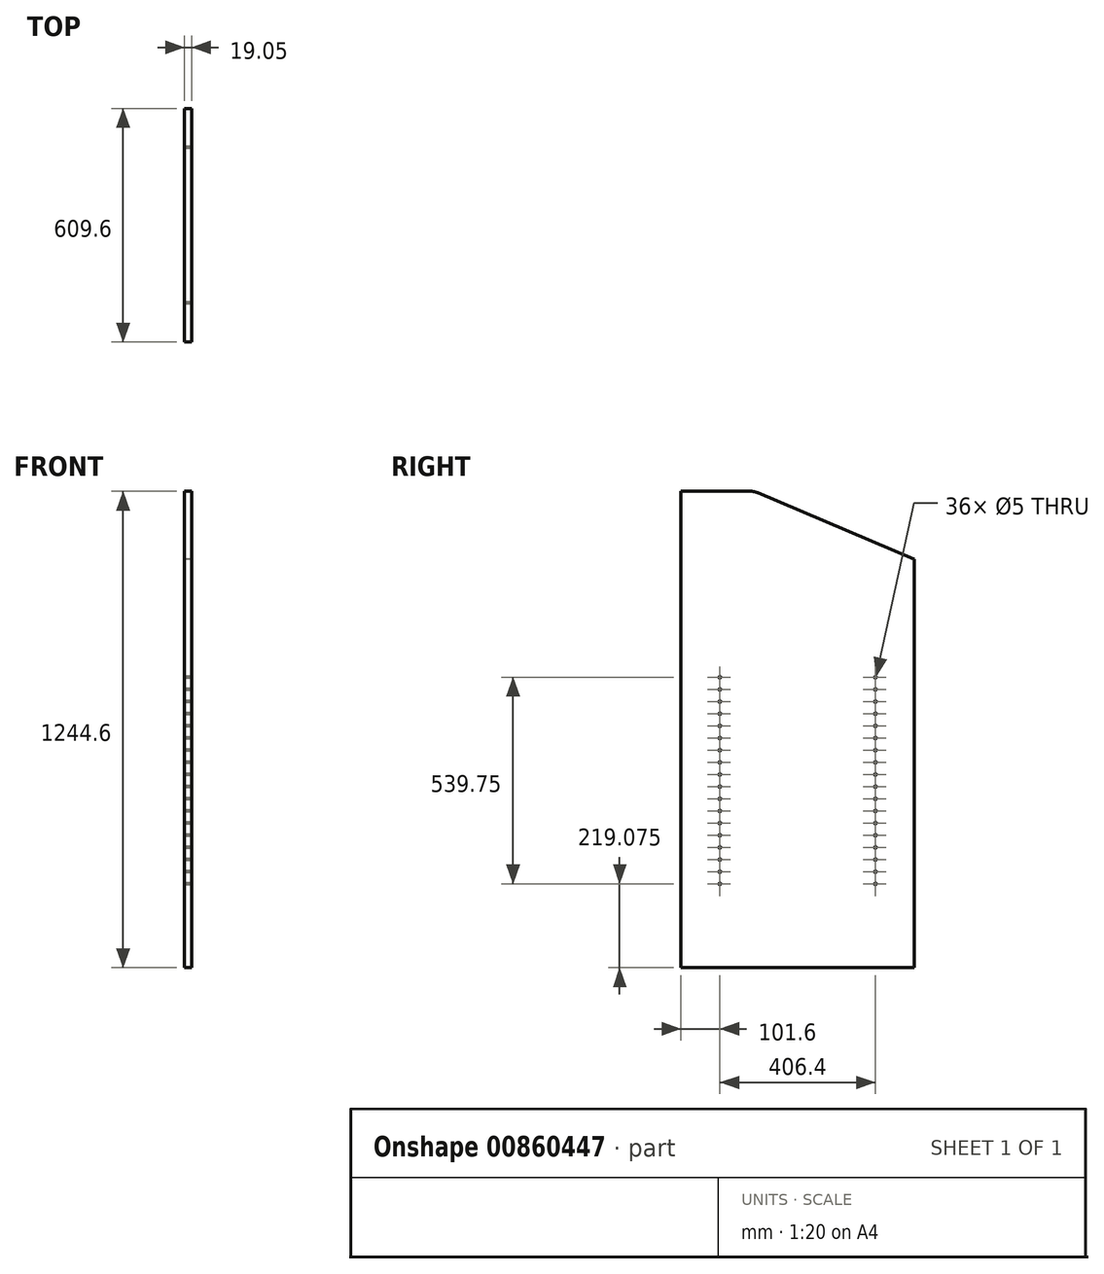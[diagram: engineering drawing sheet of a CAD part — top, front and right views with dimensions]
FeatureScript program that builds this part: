
annotation { "Feature Type Name" : "Feature", "Feature Type Description" : "" }
export const myFeature = defineFeature(function(context is Context, id is Id, definition is map)
    precondition{}
    {
        {
            var Q0;
            Q0=qCreatedBy(makeId("Right.planeOp"),FACE);
            var sketch = newSketch(context, id + "F0", { "sketchPlane" : qUnion([Q0])});
            skLineSegment(sketch, "E0.bottom", {"start": v(304.8, 622.3) * mm, "end": v(-304.8, 622.3) * mm});
            skLineSegment(sketch, "E0.top", {"start": v(304.8, -622.3) * mm, "end": v(-304.8, -622.3) * mm});
            skLineSegment(sketch, "E0.left", {"start": v(304.8, 622.3) * mm, "end": v(304.8, -622.3) * mm});
            skLineSegment(sketch, "E0.right", {"start": v(-304.8, 622.3) * mm, "end": v(-304.8, -622.3) * mm});
            skPoint(sketch, "E0.middle", {"position": v(0, 0) * mm});
            skLineSegment(sketch, "E1", {"start": v(304.8, 622.3) * mm, "end": v(124.63, 622.3) * mm});
            skLineSegment(sketch, "E2", {"start": v(-304.8, 622.3) * mm, "end": v(-304.8, 444.5) * mm});
            skLineSegment(sketch, "E3", {"start": v(-304.8, 444.5) * mm, "end": v(104.8, 618.27) * mm});
            skPoint(sketch, "E4.visualSharp", {"position": v(114.3, 622.3) * mm});
            skArc(sketch, "E4.filletArc", {"start": v(124.63, 622.3) * mm, "mid": v(114.5, 621.28) * mm, "end": v(104.8, 618.27) * mm});
            skLineSegment(sketch, "E5", {"start": v(-304.8, 444.5) * mm, "end": v(-304.8, 396.87) * mm});
            skSolve(sketch);
        }
        {
            var Q0;
            Q0=makeQuery(id+"F0.imprint","IMPRINT",FACE,{"disambiguationData":[TD([[makeQuery(id+"F0.imprint","IMPRINT",EDGE,{"derivedFrom":sQuery(id+"F0.wireOp",EDGE,"E0.top")}),-1.0]])]});
            extrude(context, id + "F1", {"entities" : qUnion([Q0]), "depth" : 19.05 * mm, "offsetDistance" : 25.4 * mm});
        }
        {
            var Q0;
            Q0=makeQuery(id+"F1.opExtrude","CAP_FACE",FACE,{"disambiguationData":[OSD([sQuery(id+"F0.wireOp",EDGE,"E0.top"),sQuery(id+"F0.wireOp",EDGE,"E0.left"),sQuery(id+"F0.wireOp",EDGE,"E0.right"),sQuery(id+"F0.wireOp",EDGE,"E1"),sQuery(id+"F0.wireOp",EDGE,"E3"),sQuery(id+"F0.wireOp",EDGE,"E4.filletArc"),sQuery(id+"F0.wireOp",EDGE,"E5")])],"isStart":false});
            var sketch = newSketch(context, id + "F2", { "sketchPlane" : qUnion([Q0])});
            skLineSegment(sketch, "E6", {"start": v(0, -622.3) * mm, "end": v(0, -387.35) * mm});
            skLineSegment(sketch, "E7.bottom", {"start": v(203.2, -371.48) * mm, "end": v(-203.2, -371.48) * mm});
            skLineSegment(sketch, "E7.top", {"start": v(203.2, -403.23) * mm, "end": v(-203.2, -403.23) * mm});
            skLineSegment(sketch, "E7.left", {"start": v(203.2, -371.48) * mm, "end": v(203.2, -403.23) * mm});
            skLineSegment(sketch, "E7.right", {"start": v(-203.2, -371.48) * mm, "end": v(-203.2, -403.23) * mm});
            skPoint(sketch, "E7.middle", {"position": v(0, -387.35) * mm});
            skLineSegment(sketch, "E8.bottom", {"start": v(203.2, -339.73) * mm, "end": v(-203.2, -339.73) * mm});
            skLineSegment(sketch, "E8.top", {"start": v(203.2, -307.98) * mm, "end": v(-203.2, -307.98) * mm});
            skLineSegment(sketch, "E8.left", {"start": v(203.2, -339.73) * mm, "end": v(203.2, -307.98) * mm});
            skLineSegment(sketch, "E8.right", {"start": v(-203.2, -339.73) * mm, "end": v(-203.2, -307.98) * mm});
            skPoint(sketch, "E8.middle", {"position": v(0, -323.85) * mm});
            skLineSegment(sketch, "E9", {"start": v(0, -323.85) * mm, "end": v(0, -260.35) * mm});
            skLineSegment(sketch, "E10.bottom", {"start": v(203.2, -276.23) * mm, "end": v(-203.2, -276.23) * mm});
            skLineSegment(sketch, "E10.top", {"start": v(203.2, -244.48) * mm, "end": v(-203.2, -244.48) * mm});
            skLineSegment(sketch, "E10.left", {"start": v(203.2, -276.23) * mm, "end": v(203.2, -244.48) * mm});
            skLineSegment(sketch, "E10.right", {"start": v(-203.2, -276.23) * mm, "end": v(-203.2, -244.48) * mm});
            skPoint(sketch, "E10.middle", {"position": v(0, -260.35) * mm});
            skLineSegment(sketch, "E11", {"start": v(0, -260.35) * mm, "end": v(0, -196.85) * mm});
            skLineSegment(sketch, "E12.bottom", {"start": v(-203.2, -212.73) * mm, "end": v(203.2, -212.73) * mm});
            skLineSegment(sketch, "E12.top", {"start": v(-203.2, -180.98) * mm, "end": v(203.2, -180.98) * mm});
            skLineSegment(sketch, "E12.left", {"start": v(-203.2, -212.73) * mm, "end": v(-203.2, -180.98) * mm});
            skLineSegment(sketch, "E12.right", {"start": v(203.2, -212.73) * mm, "end": v(203.2, -180.98) * mm});
            skPoint(sketch, "E12.middle", {"position": v(0, -196.85) * mm});
            skLineSegment(sketch, "E13", {"start": v(0, -196.85) * mm, "end": v(0, -133.35) * mm});
            skLineSegment(sketch, "E14.bottom", {"start": v(-203.2, -149.23) * mm, "end": v(203.2, -149.23) * mm});
            skLineSegment(sketch, "E14.top", {"start": v(-203.2, -117.48) * mm, "end": v(203.2, -117.48) * mm});
            skLineSegment(sketch, "E14.left", {"start": v(-203.2, -149.23) * mm, "end": v(-203.2, -117.48) * mm});
            skLineSegment(sketch, "E14.right", {"start": v(203.2, -149.23) * mm, "end": v(203.2, -117.48) * mm});
            skPoint(sketch, "E14.middle", {"position": v(0, -133.35) * mm});
            skLineSegment(sketch, "E15", {"start": v(0, -133.35) * mm, "end": v(0, -69.85) * mm});
            skLineSegment(sketch, "E16.bottom", {"start": v(-203.2, -85.73) * mm, "end": v(203.2, -85.73) * mm});
            skLineSegment(sketch, "E16.top", {"start": v(-203.2, -53.98) * mm, "end": v(203.2, -53.98) * mm});
            skLineSegment(sketch, "E16.left", {"start": v(-203.2, -85.73) * mm, "end": v(-203.2, -53.98) * mm});
            skLineSegment(sketch, "E16.right", {"start": v(203.2, -85.73) * mm, "end": v(203.2, -53.98) * mm});
            skPoint(sketch, "E16.middle", {"position": v(0, -69.85) * mm});
            skLineSegment(sketch, "E17", {"start": v(0, -69.85) * mm, "end": v(0, -6.35) * mm});
            skLineSegment(sketch, "E18.bottom", {"start": v(-203.2, -22.23) * mm, "end": v(203.2, -22.23) * mm});
            skLineSegment(sketch, "E18.top", {"start": v(-203.2, 9.52) * mm, "end": v(203.2, 9.52) * mm});
            skLineSegment(sketch, "E18.left", {"start": v(-203.2, -22.23) * mm, "end": v(-203.2, 9.52) * mm});
            skLineSegment(sketch, "E18.right", {"start": v(203.2, -22.23) * mm, "end": v(203.2, 9.52) * mm});
            skPoint(sketch, "E18.middle", {"position": v(0, -6.35) * mm});
            skLineSegment(sketch, "E19", {"start": v(0, -6.35) * mm, "end": v(0, 57.15) * mm});
            skLineSegment(sketch, "E20.bottom", {"start": v(-203.2, 73.02) * mm, "end": v(203.2, 73.02) * mm});
            skLineSegment(sketch, "E20.top", {"start": v(-203.2, 41.27) * mm, "end": v(203.2, 41.27) * mm});
            skLineSegment(sketch, "E20.left", {"start": v(-203.2, 73.02) * mm, "end": v(-203.2, 41.27) * mm});
            skLineSegment(sketch, "E20.right", {"start": v(203.2, 73.02) * mm, "end": v(203.2, 41.27) * mm});
            skPoint(sketch, "E20.middle", {"position": v(0, 57.15) * mm});
            skLineSegment(sketch, "E21", {"start": v(0, 57.15) * mm, "end": v(0, 120.65) * mm});
            skLineSegment(sketch, "E22.bottom", {"start": v(-203.2, 104.77) * mm, "end": v(203.2, 104.77) * mm});
            skLineSegment(sketch, "E22.top", {"start": v(-203.2, 136.52) * mm, "end": v(203.2, 136.52) * mm});
            skLineSegment(sketch, "E22.left", {"start": v(-203.2, 104.77) * mm, "end": v(-203.2, 136.52) * mm});
            skLineSegment(sketch, "E22.right", {"start": v(203.2, 104.77) * mm, "end": v(203.2, 136.52) * mm});
            skPoint(sketch, "E22.middle", {"position": v(0, 120.65) * mm});
            skSolve(sketch);
        }
        {
            var Q0;
            Q0=sQuery(id+"F2.wireOp",VERTEX,"E22.top.start");
            var Q1;
            Q1=sQuery(id+"F2.wireOp",VERTEX,"E22.bottom.start");
            var Q2;
            Q2=sQuery(id+"F2.wireOp",VERTEX,"E20.bottom.start");
            var Q3;
            Q3=sQuery(id+"F2.wireOp",VERTEX,"E20.top.start");
            var Q4;
            Q4=sQuery(id+"F2.wireOp",VERTEX,"E18.top.start");
            var Q5;
            Q5=sQuery(id+"F2.wireOp",VERTEX,"E18.bottom.start");
            var Q6;
            Q6=sQuery(id+"F2.wireOp",VERTEX,"E16.top.start");
            var Q7;
            Q7=sQuery(id+"F2.wireOp",VERTEX,"E16.bottom.start");
            var Q8;
            Q8=sQuery(id+"F2.wireOp",VERTEX,"E14.top.start");
            var Q9;
            Q9=sQuery(id+"F2.wireOp",VERTEX,"E14.bottom.start");
            var Q10;
            Q10=sQuery(id+"F2.wireOp",VERTEX,"E12.top.start");
            var Q11;
            Q11=sQuery(id+"F2.wireOp",VERTEX,"E12.bottom.start");
            var Q12;
            Q12=sQuery(id+"F2.wireOp",VERTEX,"E10.top.end");
            var Q13;
            Q13=sQuery(id+"F2.wireOp",VERTEX,"E10.bottom.end");
            var Q14;
            Q14=sQuery(id+"F2.wireOp",VERTEX,"E8.top.end");
            var Q15;
            Q15=sQuery(id+"F2.wireOp",VERTEX,"E8.bottom.end");
            var Q16;
            Q16=sQuery(id+"F2.wireOp",VERTEX,"E7.bottom.end");
            var Q17;
            Q17=sQuery(id+"F2.wireOp",VERTEX,"E7.top.end");
            var Q18;
            Q18=sQuery(id+"F2.wireOp",VERTEX,"E7.top.start");
            var Q19;
            Q19=sQuery(id+"F2.wireOp",VERTEX,"E7.bottom.start");
            var Q20;
            Q20=sQuery(id+"F2.wireOp",VERTEX,"E8.bottom.start");
            var Q21;
            Q21=sQuery(id+"F2.wireOp",VERTEX,"E8.top.start");
            var Q22;
            Q22=sQuery(id+"F2.wireOp",VERTEX,"E10.bottom.start");
            var Q23;
            Q23=sQuery(id+"F2.wireOp",VERTEX,"E10.top.start");
            var Q24;
            Q24=sQuery(id+"F2.wireOp",VERTEX,"E12.bottom.end");
            var Q25;
            Q25=sQuery(id+"F2.wireOp",VERTEX,"E12.top.end");
            var Q26;
            Q26=sQuery(id+"F2.wireOp",VERTEX,"E14.bottom.end");
            var Q27;
            Q27=sQuery(id+"F2.wireOp",VERTEX,"E14.top.end");
            var Q28;
            Q28=sQuery(id+"F2.wireOp",VERTEX,"E16.bottom.end");
            var Q29;
            Q29=sQuery(id+"F2.wireOp",VERTEX,"E16.top.end");
            var Q30;
            Q30=sQuery(id+"F2.wireOp",VERTEX,"E18.bottom.end");
            var Q31;
            Q31=sQuery(id+"F2.wireOp",VERTEX,"E18.top.end");
            var Q32;
            Q32=sQuery(id+"F2.wireOp",VERTEX,"E20.top.end");
            var Q33;
            Q33=sQuery(id+"F2.wireOp",VERTEX,"E20.bottom.end");
            var Q34;
            Q34=sQuery(id+"F2.wireOp",VERTEX,"E22.bottom.end");
            var Q35;
            Q35=sQuery(id+"F2.wireOp",VERTEX,"E22.top.end");
            var Q36;
            Q36=makeQuery(id+"F1.opExtrude","SWEPT_BODY",BODY,{"disambiguationData":[OSD([sQuery(id+"F0.wireOp",EDGE,"E0.top"),sQuery(id+"F0.wireOp",EDGE,"E0.left"),sQuery(id+"F0.wireOp",EDGE,"E0.right"),sQuery(id+"F0.wireOp",EDGE,"E1"),sQuery(id+"F0.wireOp",EDGE,"E3"),sQuery(id+"F0.wireOp",EDGE,"E4.filletArc"),sQuery(id+"F0.wireOp",EDGE,"E5")])]});
            hole(context, id + "F3", {"style" : HoleStyle.SIMPLE, "endStyle" : HoleEndStyle.BLIND, "holeDiameter" : 5 * mm, "majorDiameter" : 6.35 * mm, "holeDepth" : 14.22 * mm, "isTappedThrough" : true, "tappedDepth" : 12.7 * mm, "tapClearance" : 3, "locations" : qUnion([Q0, Q1, Q2, Q3, Q4, Q5, Q6, Q7, Q8, Q9, Q10, Q11, Q12, Q13, Q14, Q15, Q16, Q17, Q18, Q19, Q20, Q21, Q22, Q23, Q24, Q25, Q26, Q27, Q28, Q29, Q30, Q31, Q32, Q33, Q34, Q35]), "scope" : qUnion([Q36]), "startStyle" : HoleStartStyle.SKETCH});
        }
        {
            var Q0;
            Q0=makeQuery(id+"F1.opExtrude","SWEPT_BODY",BODY,{"disambiguationData":[OSD([sQuery(id+"F0.wireOp",EDGE,"E0.top"),sQuery(id+"F0.wireOp",EDGE,"E0.left"),sQuery(id+"F0.wireOp",EDGE,"E0.right"),sQuery(id+"F0.wireOp",EDGE,"E1"),sQuery(id+"F0.wireOp",EDGE,"E3"),sQuery(id+"F0.wireOp",EDGE,"E4.filletArc"),sQuery(id+"F0.wireOp",EDGE,"E5")])]});
            var Q1;
            Q1=makeQuery(id+"F1.opExtrude","SWEPT_FACE",FACE,{"disambiguationData":[OSD([sQuery(id+"F0.wireOp",EDGE,"E0.left")])]});
            mirror(context, id + "F4", {"entities" : qUnion([Q0]), "mirrorPlane" : qUnion([Q1])});
        }
        {
            var Q0;
            Q0=makeQuery(id+"F1.opExtrude","SWEPT_BODY",BODY,{"disambiguationData":[OSD([sQuery(id+"F0.wireOp",EDGE,"E0.top"),sQuery(id+"F0.wireOp",EDGE,"E0.left"),sQuery(id+"F0.wireOp",EDGE,"E0.right"),sQuery(id+"F0.wireOp",EDGE,"E1"),sQuery(id+"F0.wireOp",EDGE,"E3"),sQuery(id+"F0.wireOp",EDGE,"E4.filletArc"),sQuery(id+"F0.wireOp",EDGE,"E5")])]});
            deleteBodies(context, id + "F5", {"entities" : qUnion([Q0])});
        }
    });
